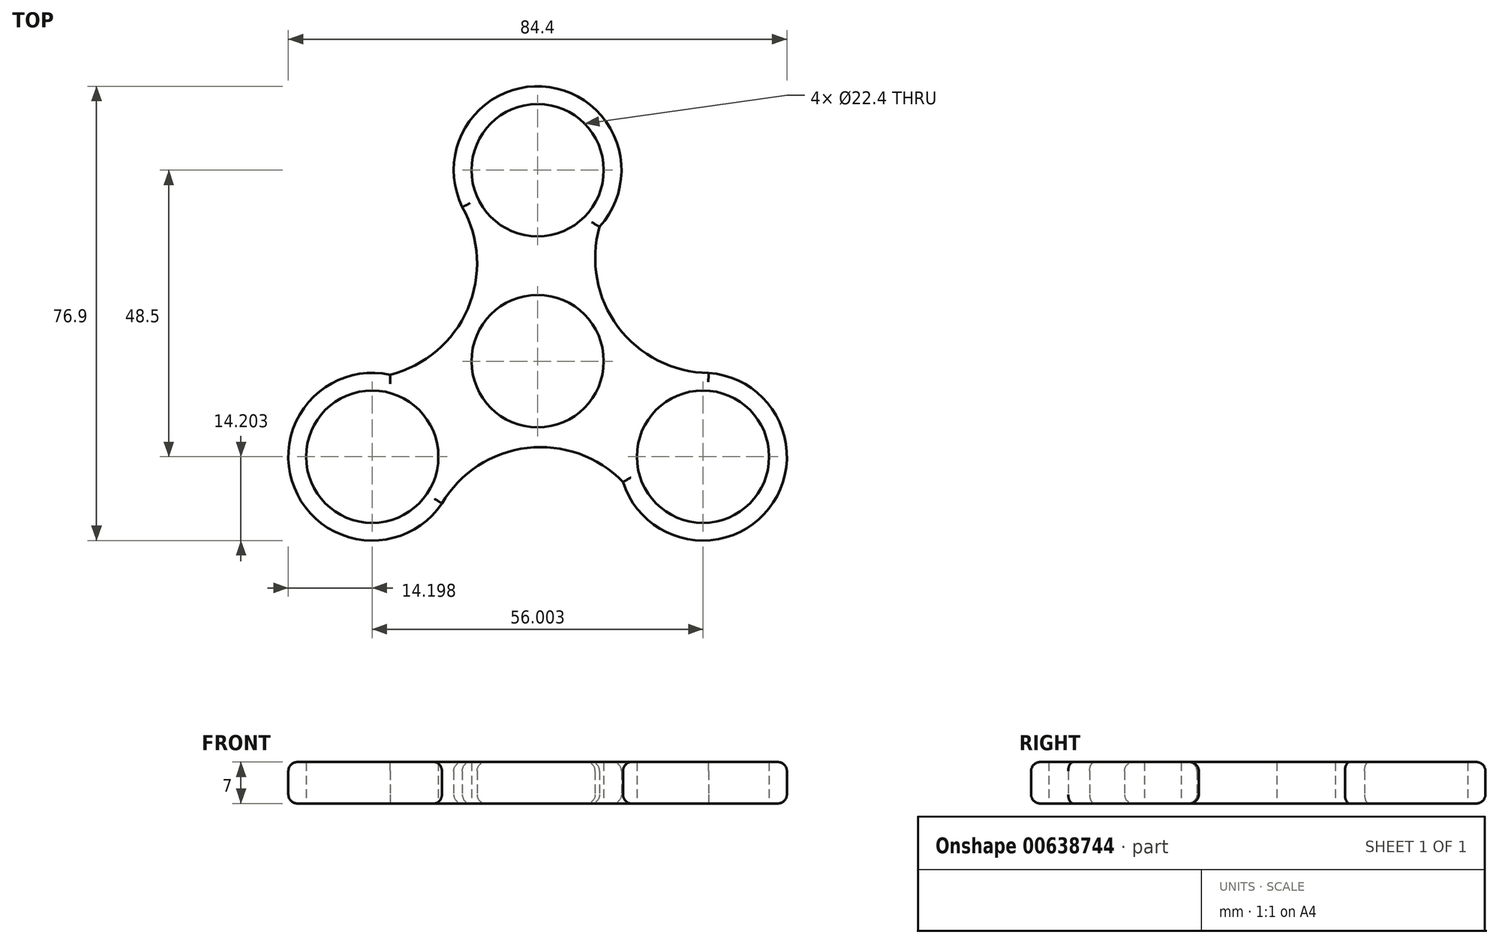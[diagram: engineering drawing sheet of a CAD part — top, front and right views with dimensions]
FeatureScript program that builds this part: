
annotation { "Feature Type Name" : "Feature", "Feature Type Description" : "" }
export const myFeature = defineFeature(function(context is Context, id is Id, definition is map)
    precondition{}
    {
        {
            var Q0;
            Q0=qCreatedBy(makeId("Top.planeOp"),FACE);
            var sketch = newSketch(context, id + "F0", { "sketchPlane" : qUnion([Q0])});
            skCircle(sketch, "E0", {"center": v(0, 0) * mm, "radius": 11.2 * mm});
            skCircle(sketch, "E1", {"center": v(0, 32.33) * mm, "radius": 11.2 * mm});
            skArc(sketch, "E2", {"start": v(10.5, 22.76) * mm, "mid": v(1.55, 46.45) * mm, "end": v(-12.31, 25.26) * mm});
            skArc(sketch, "E3.1.0", {"start": v(-24.96, -2.3) * mm, "mid": v(-41, -21.88) * mm, "end": v(-15.72, -23.3) * mm});
            skCircle(sketch, "E3.1.1", {"center": v(-28, -16.17) * mm, "radius": 11.2 * mm});
            skArc(sketch, "E3.2.0", {"start": v(14.47, -20.47) * mm, "mid": v(39.45, -24.56) * mm, "end": v(28.03, -1.97) * mm});
            skCircle(sketch, "E3.2.1", {"center": v(28, -16.17) * mm, "radius": 11.2 * mm});
            skArc(sketch, "E4", {"start": v(-24.96, -2.3) * mm, "mid": v(-11.83, 8.87) * mm, "end": v(-12.75, 26.08) * mm});
            skArc(sketch, "E5.1.0", {"start": v(14.47, -20.47) * mm, "mid": v(-1.77, -14.68) * mm, "end": v(-16.21, -24.08) * mm});
            skArc(sketch, "E5.2.0", {"start": v(10.5, 22.76) * mm, "mid": v(13.6, 5.81) * mm, "end": v(28.96, -2) * mm});
            skSolve(sketch);
        }
        {
            var Q0;
            Q0=makeQuery(id+"F0.imprint","IMPRINT",FACE,{"disambiguationData":[TD([[makeQuery(id+"F0.imprint","IMPRINT",EDGE,{"derivedFrom":sQuery(id+"F0.wireOp",EDGE,"E0")}),-1.0]])]});
            extrude(context, id + "F1", {"entities" : qUnion([Q0]), "depth" : 7 * mm, "offsetDistance" : 25 * mm});
        }
        {
            var Q0;
            Q0=makeQuery(id+"F1.opExtrude","CAP_EDGE",EDGE,{"disambiguationData":[OSD([sQuery(id+"F0.wireOp",EDGE,"E2")])],"isStart":false});
            var Q1;
            Q1=makeQuery(id+"F1.opExtrude","CAP_EDGE",EDGE,{"disambiguationData":[OSD([sQuery(id+"F0.wireOp",EDGE,"E5.2.0")])],"isStart":false});
            var Q2;
            Q2=makeQuery(id+"F1.opExtrude","CAP_EDGE",EDGE,{"disambiguationData":[OSD([sQuery(id+"F0.wireOp",EDGE,"E3.2.0")])],"isStart":false});
            var Q3;
            Q3=makeQuery(id+"F1.opExtrude","CAP_EDGE",EDGE,{"disambiguationData":[OSD([sQuery(id+"F0.wireOp",EDGE,"E5.1.0")])],"isStart":false});
            var Q4;
            Q4=makeQuery(id+"F1.opExtrude","CAP_EDGE",EDGE,{"disambiguationData":[OSD([sQuery(id+"F0.wireOp",EDGE,"E3.1.0")])],"isStart":false});
            var Q5;
            Q5=makeQuery(id+"F1.opExtrude","CAP_EDGE",EDGE,{"disambiguationData":[OSD([sQuery(id+"F0.wireOp",EDGE,"E4")])],"isStart":false});
            fillet(context, id + "F2", {"entities" : qUnion([Q0, Q1, Q2, Q3, Q4, Q5]), "radius" : 1.5 * mm, "tangentPropagation" : true, "allowEdgeOverflow" : false});
        }
        {
            var Q0;
            Q0=makeQuery(id+"F1.opExtrude","CAP_EDGE",EDGE,{"disambiguationData":[OSD([sQuery(id+"F0.wireOp",EDGE,"E2")])],"isStart":true});
            var Q1;
            Q1=makeQuery(id+"F1.opExtrude","CAP_EDGE",EDGE,{"disambiguationData":[OSD([sQuery(id+"F0.wireOp",EDGE,"E5.2.0")])],"isStart":true});
            var Q2;
            Q2=makeQuery(id+"F1.opExtrude","CAP_EDGE",EDGE,{"disambiguationData":[OSD([sQuery(id+"F0.wireOp",EDGE,"E3.2.0")])],"isStart":true});
            var Q3;
            Q3=makeQuery(id+"F1.opExtrude","CAP_EDGE",EDGE,{"disambiguationData":[OSD([sQuery(id+"F0.wireOp",EDGE,"E5.1.0")])],"isStart":true});
            var Q4;
            Q4=makeQuery(id+"F1.opExtrude","CAP_EDGE",EDGE,{"disambiguationData":[OSD([sQuery(id+"F0.wireOp",EDGE,"E3.1.0")])],"isStart":true});
            var Q5;
            Q5=makeQuery(id+"F1.opExtrude","CAP_EDGE",EDGE,{"disambiguationData":[OSD([sQuery(id+"F0.wireOp",EDGE,"E4")])],"isStart":true});
            fillet(context, id + "F3", {"entities" : qUnion([Q0, Q1, Q2, Q3, Q4, Q5]), "radius" : 1.5 * mm, "tangentPropagation" : true, "allowEdgeOverflow" : false});
        }
    });
